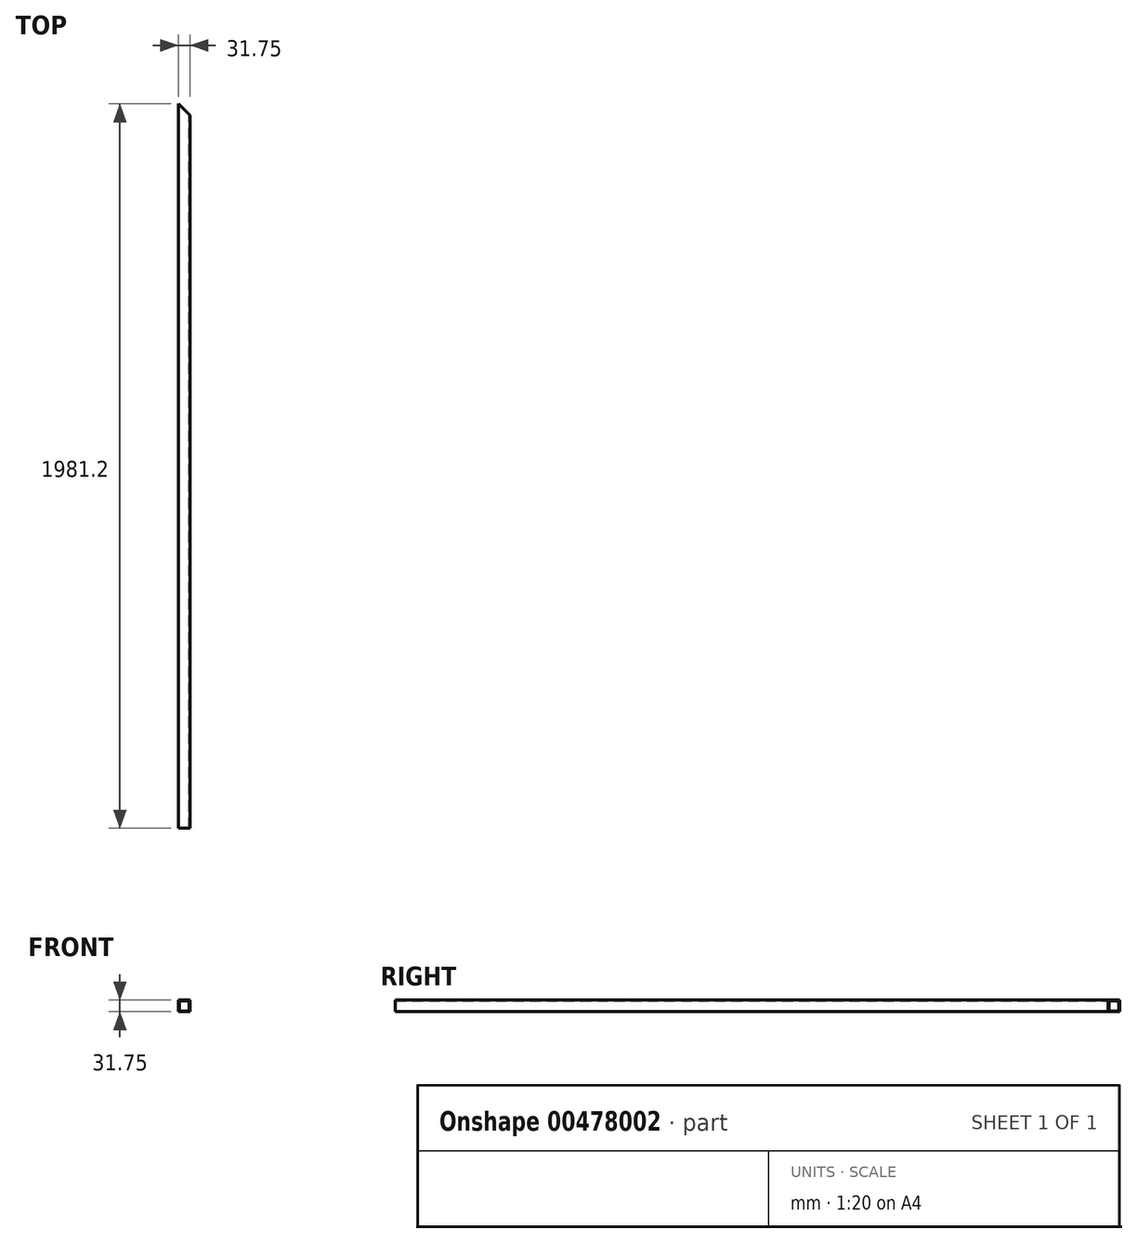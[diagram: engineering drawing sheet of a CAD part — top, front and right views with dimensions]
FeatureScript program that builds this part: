
annotation { "Feature Type Name" : "Feature", "Feature Type Description" : "" }
export const myFeature = defineFeature(function(context is Context, id is Id, definition is map)
    precondition{}
    {
        {
            var Q0;
            Q0=qCreatedBy(makeId("Front.planeOp"),FACE);
            var sketch = newSketch(context, id + "F0", { "sketchPlane" : qUnion([Q0])});
            skLineSegment(sketch, "E0.bottom", {"start": v(-64.17, 32) * mm, "end": v(-32.42, 32) * mm});
            skLineSegment(sketch, "E0.top", {"start": v(-64.17, 0.25) * mm, "end": v(-32.42, 0.25) * mm});
            skLineSegment(sketch, "E0.left", {"start": v(-64.17, 32) * mm, "end": v(-64.17, 0.25) * mm});
            skLineSegment(sketch, "E0.right", {"start": v(-32.42, 32) * mm, "end": v(-32.42, 0.25) * mm});
            skLineSegment(sketch, "E1.0", {"start": v(-34.53, 29.89) * mm, "end": v(-34.53, 2.35) * mm});
            skLineSegment(sketch, "E1.1", {"start": v(-62.06, 29.89) * mm, "end": v(-34.53, 29.89) * mm});
            skLineSegment(sketch, "E1.2", {"start": v(-62.06, 29.89) * mm, "end": v(-62.06, 2.35) * mm});
            skLineSegment(sketch, "E1.3", {"start": v(-62.06, 2.35) * mm, "end": v(-34.53, 2.35) * mm});
            skSolve(sketch);
        }
        {
            var Q0;
            Q0=qSketchRegion(id+"F0",true);
            extrude(context, id + "F1", {"entities" : qUnion([Q0]), "depth" : 1981.2 * mm});
        }
        {
            var Q0;
            Q0=makeQuery(id+"F1.opExtrude","SWEPT_FACE",FACE,{"disambiguationData":[OSD([sQuery(id+"F0.wireOp",EDGE,"E0.bottom")])]});
            var sketch = newSketch(context, id + "F2", { "sketchPlane" : qUnion([Q0])});
            skLineSegment(sketch, "E2", {"start": v(-64.17, 0) * mm, "end": v(-32.42, -31.75) * mm});
            skSolve(sketch);
        }
        {
            var Q0;
            Q0=qSketchRegion(id+"F2",true);
            var Q1;
            {var subQ0=sQuery(id+"F2.wireOp",EDGE,"E2");Q1=makeQuery(id+"F2.imprint","IMPRINT",FACE,{"disambiguationData":[TD([[makeQuery(id+"F2.imprint","IMPRINT",EDGE,{"derivedFrom":subQ0}),1.0]])]});}
            extrude(context, id + "F3", {"entities" : qUnion([Q0, Q1]), "operationType" : NewBodyOperationType.REMOVE, "oppositeDirection" : true, "depth" : 76.2 * mm});
        }
    });
